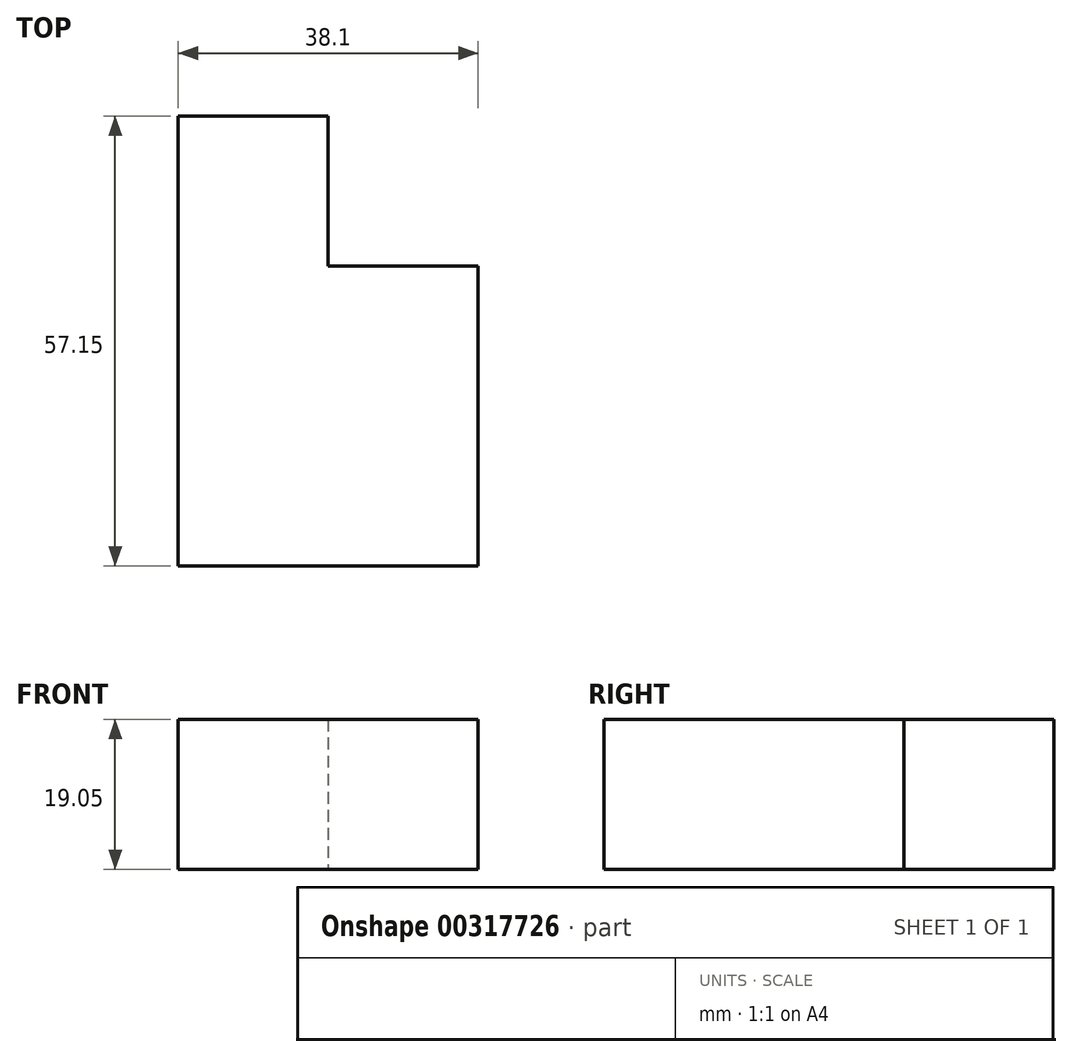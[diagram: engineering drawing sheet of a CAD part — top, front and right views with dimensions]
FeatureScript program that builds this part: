
annotation { "Feature Type Name" : "Feature", "Feature Type Description" : "" }
export const myFeature = defineFeature(function(context is Context, id is Id, definition is map)
    precondition{}
    {
        {
            var Q0;
            Q0=qCreatedBy(makeId("Top.planeOp"),FACE);
            var sketch = newSketch(context, id + "F0", { "sketchPlane" : qUnion([Q0])});
            skLineSegment(sketch, "E0.bottom", {"start": v(0, 0) * mm, "end": v(38.1, 0) * mm});
            skLineSegment(sketch, "E0.top", {"start": v(19.05, 38.1) * mm, "end": v(38.1, 38.1) * mm});
            skLineSegment(sketch, "E0.left", {"start": v(0, 0) * mm, "end": v(0, 38.1) * mm});
            skLineSegment(sketch, "E0.right", {"start": v(38.1, 0) * mm, "end": v(38.1, 38.1) * mm});
            skLineSegment(sketch, "E1", {"start": v(19.05, 38.1) * mm, "end": v(19.05, 57.15) * mm});
            skLineSegment(sketch, "E2", {"start": v(19.05, 57.15) * mm, "end": v(0, 57.15) * mm});
            skLineSegment(sketch, "E3", {"start": v(0, 57.15) * mm, "end": v(0, 38.1) * mm});
            skSolve(sketch);
        }
        {
            var Q0;
            Q0 = qSketchRegion(id + "F0", true);
            extrude(context, id + "F1", {"entities" : qUnion([Q0]), "depth" : 19.05 * mm});
        }
    });
